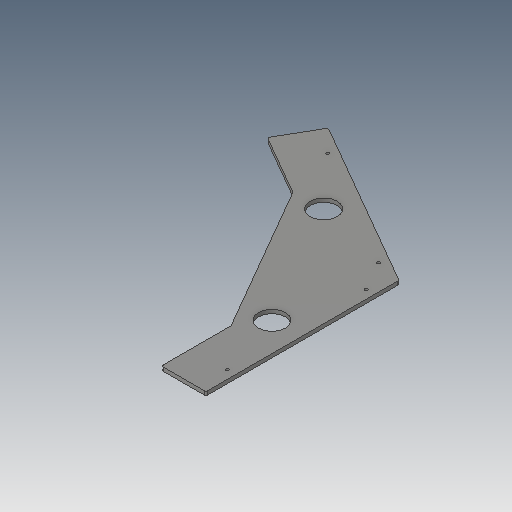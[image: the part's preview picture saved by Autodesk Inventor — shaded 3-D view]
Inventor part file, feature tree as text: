
AUTODESK INVENTOR PART (.ipt)
format: ipt  version: 2023.5 (Build 275446000, 446)  size: 99,328 bytes
history: native  units: in
note: dims shown in document units (in); Inventor stores cm internally (conversion verified against a paired STEP export)
features: fillet x1
ambient origin geometry x8: Origin, YZ Plane, XZ Plane, XY Plane, X Axis, Y Axis, Z Axis, Center Point
bodies: Solid1 (feature_tree)
feature tree (1):
  fillet  "Fillet1"  [1 undecoded]
note: 1 required parameter value undecoded (feature->parameter linkage not recoverable at this tier; creation-order binding heuristic only, values carry confidence <= 0.55)
